# Revit family: Electronics_Commercial-Audio_Biamp_Amplifier_REVAMP2150
name_source: partatom
category: Communication Devices
units: mm (PartAtom-declared; Revit-internal decimal feet)

## family parameters
Cut with Voids When Loaded = No
Host = Face
Maintain Annotation Orientation = No
OmniClass Number = 23.85.10.11
OmniClass Title = Audio Information, Sound Signals
Part Type = Normal
Room Calculation Point = No
Round Connector Dimension = Use Diameter
Shared = No

## types (1)
- 2150
    Apparent Load = 400 VA
    Applicable low impedance = Yes
    Channel separation = > 70 dB @ 1 kHz
    Connector Description = 100-240VAC/50-60Hz/400W
    Cooling system = Convection
    Default Elevation = 4' - 0"
    Depth = 0' - 9 1/2"
    Description = REVAMP2150 Stereo Digital Amplifier, Convection Cooled
    Frequency response (in Hz) = 20 - 22 k
    Height = 0' - 1 1/2"
    Housing Material = Biamp - Metal - Black
    Line input balanced = 2
    Line input unbalanced = 2
    Manufacturer = Biamp
    Max Power Consumption = 400 W
    Minimum impedance load bridged per channel in ohms = 8
    Minimum impedance load per channel in ohms = 4
    Model = 2150
    Number of Poles = 1
    Output channels = 2
    Power Factor = 1
    Power amp topology = Class-D
    Power supply technology = Switching mode power supply
    Product Documentation Link = https://downloads.biamp.com
    Product Page URL = https://www.biamp.com
    Product data url = https://www.bimobject.com
    URL = https://www.biamp.com
    Voltage = 120 V
    Weight = 7.05 lb
    Width = 1' - 7"

## geometry (parser evidence)
native form markers: Sweep x1
no freeform markers — native parametric forms only
